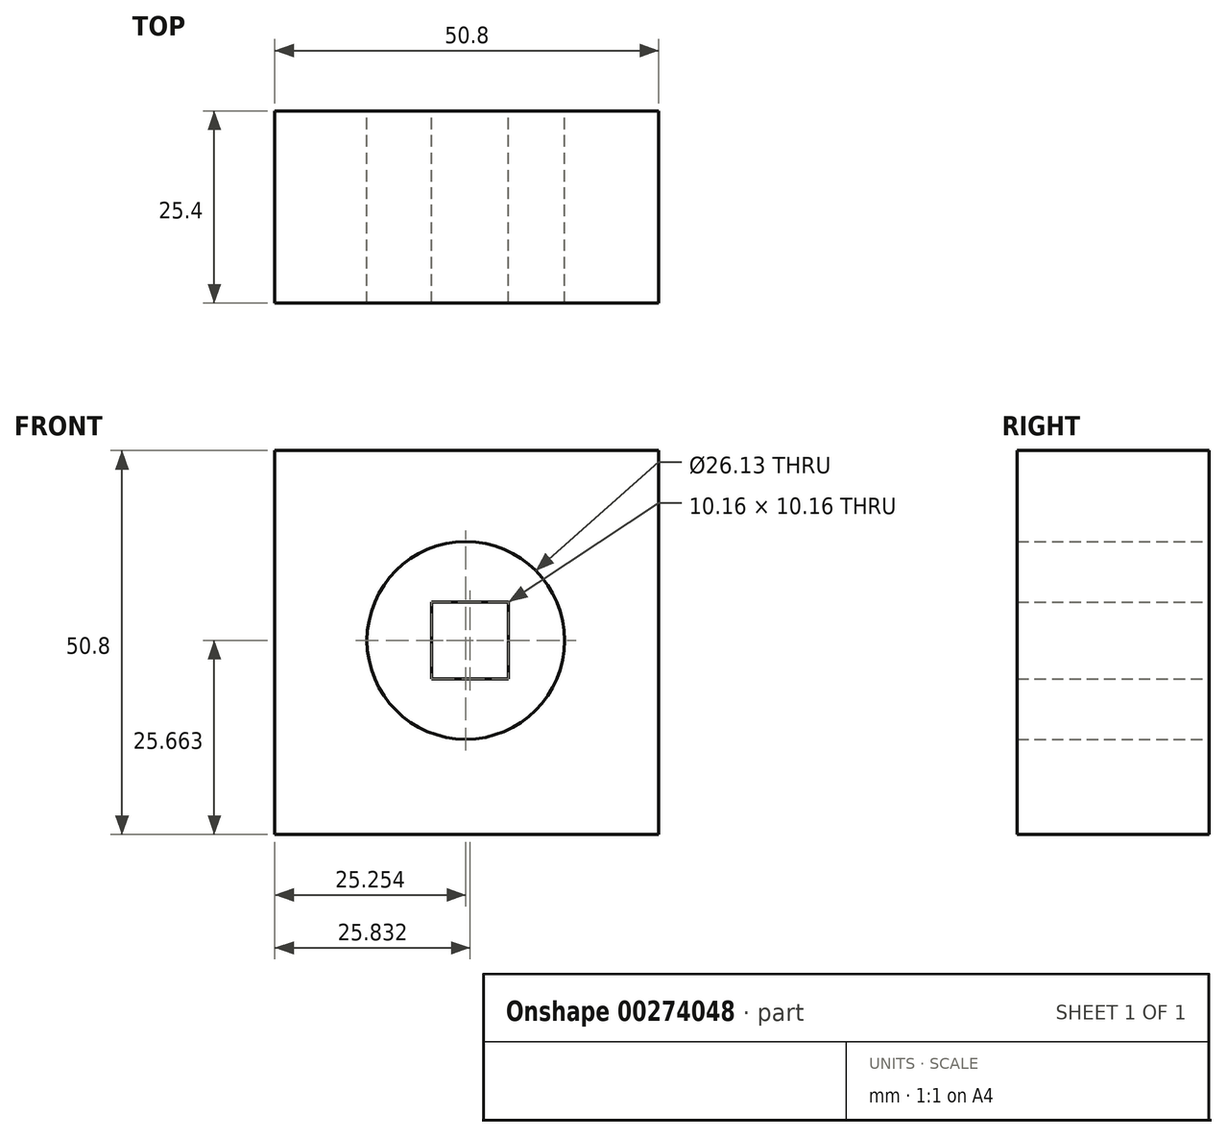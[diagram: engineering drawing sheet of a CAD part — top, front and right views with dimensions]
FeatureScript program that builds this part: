
annotation { "Feature Type Name" : "Feature", "Feature Type Description" : "" }
export const myFeature = defineFeature(function(context is Context, id is Id, definition is map)
    precondition{}
    {
        {
            var Q0;
            Q0=qCreatedBy(makeId("Front.planeOp"),FACE);
            var sketch = newSketch(context, id + "F0", { "sketchPlane" : qUnion([Q0])});
            skLineSegment(sketch, "E0.bottom", {"start": v(-44.65, 39.28) * mm, "end": v(6.15, 39.28) * mm});
            skLineSegment(sketch, "E0.top", {"start": v(-44.65, -11.52) * mm, "end": v(6.15, -11.52) * mm});
            skLineSegment(sketch, "E0.left", {"start": v(-44.65, 39.28) * mm, "end": v(-44.65, -11.52) * mm});
            skLineSegment(sketch, "E0.right", {"start": v(6.15, 39.28) * mm, "end": v(6.15, -11.52) * mm});
            skCircle(sketch, "E1", {"center": v(-19.4, 14.14) * mm, "radius": 13.06 * mm});
            skSolve(sketch);
        }
        {
            var Q0;
            Q0=makeQuery(id+"F0.imprint","IMPRINT",FACE,{"disambiguationData":[TD([[makeQuery(id+"F0.imprint","IMPRINT",EDGE,{"derivedFrom":sQuery(id+"F0.wireOp",EDGE,"E0.bottom")}),-1.0]])]});
            extrude(context, id + "F1", {"entities" : qUnion([Q0]), "depth" : 25.4 * mm});
        }
        {
            var Q0;
            Q0=makeQuery(id+"F0.imprint","IMPRINT",FACE,{"disambiguationData":[TD([[makeQuery(id+"F0.imprint","IMPRINT",EDGE,{"derivedFrom":sQuery(id+"F0.wireOp",EDGE,"E1")}),1.0]])]});
            extrude(context, id + "F2", {"entities" : qUnion([Q0]), "depth" : 25.4 * mm});
        }
        {
            var Q0;
            Q0=makeQuery(id+"F0.imprint","IMPRINT",FACE,{"disambiguationData":[TD([[makeQuery(id+"F0.imprint","IMPRINT",EDGE,{"derivedFrom":sQuery(id+"F0.wireOp",EDGE,"E1")}),1.0]])]});
            var sketch = newSketch(context, id + "F3", { "sketchPlane" : qUnion([Q0])});
            skLineSegment(sketch, "E2.bottom", {"start": v(-23.9, 9.06) * mm, "end": v(-13.74, 9.06) * mm});
            skLineSegment(sketch, "E2.top", {"start": v(-23.9, 19.22) * mm, "end": v(-13.74, 19.22) * mm});
            skLineSegment(sketch, "E2.left", {"start": v(-23.9, 9.06) * mm, "end": v(-23.9, 19.22) * mm});
            skLineSegment(sketch, "E2.right", {"start": v(-13.74, 9.06) * mm, "end": v(-13.74, 19.22) * mm});
            skPoint(sketch, "E2.middle", {"position": v(-18.82, 14.14) * mm});
            skSolve(sketch);
        }
        {
            var Q0;
            Q0 = qSketchRegion(id + "F3", true);
            extrude(context, id + "F4", {"entities" : qUnion([Q0]), "operationType" : NewBodyOperationType.REMOVE, "depth" : 25.4 * mm});
        }
    });
